# Revit family: Top hung and pivot window FAKRO FPU-V U5 preSelect
name_source: partatom
category: Okna
revit_build: Autodesk Revit 2015 (Build: 20140606_1530(x64)
units: mm (PartAtom-declared; Revit-internal decimal feet)

## types (9) — shared parameters
Apron Material = Fakro - aluminium RAL7022
Bimobject Category = Windows - Roof Windows
CSI MasterFormat 2016 Code = 08 60 00
CSI MasterFormat 2016 Title = Roof Windows and Skylights
CSI UniFormat II Code = B3020
CSI UniFormat II Title = Roof Openings
Glazing = Fakro - Glass
Handle Material = Fakro - handle
IFC Classification = Window
Kod zespołu = B3020110
Material External = Fakro - aluminium RAL7022
Material Internal = Fakro - frame - pinewood - RAL 9010
Model = FPU-V U5 preSelect
NBS Reference = 59-72
NBS Reference Description = Roof Window Units
Opis = Top hung and pivot window
Producent = FAKRO
UNSPC Category = Roofing accessories
UNSPC Code = 301516
URL = www.fakro.com
UV radiation EN 14351-1:2006+A1:2010 = 0.28
Uniclass 1.4 Code = JL11
Uniclass 1.4 Description = Rooflights/Roof windows
Uniclass 2.0 Code = PR-59-72
Uniclass 2.0 Description = Roof Window Units
Uniclass 2015 Code = Pr_30_59_72_77
Uniclass 2015 Title = Skylights
air inlet = V40P
air permeability class EN 14351-1:2006+A1:2010 = 4
colour = NCS S0502-Y (near to RAL 9010)
glass structure = 4HT-10-4H-10-4HT
glazing U-value [W/m2K] EN 14351-1:2006+A1:2010 = 0.5
impact resistance class EN 14351-1:2006+A1:2010 = 3
light transmittance factor tv EN 14351-1:2006+A1:2010 = 0.66
material = pinewood
opening method = top hung and pivot
operation mode = manual
reaction to fire EN 14351-1:2006+A1:2010 = D-s2;d2
resistance to snow load EN 14351-1:2006+A1:2010 = 4H-10-4H-10-4H
resistance to wind load EN 14351-1:2006+A1:2010 = C5/B5
roof angle = 15 – 55 (special version of the window 15 – 85)
solar factor [ g] EN 14351-1:2006+A1:2010 = 0.46
watertightness / unshielded (A) EN 14351-1:2006+A1:2010 = E900
window acoustic performance Rw [dB] EN 14351-1:2006+A1:2010 = 33(-2; -6)
window heat transfer coefficient Uw [W/m2K] EN 14351-1:2006+A1:2010 = 0.97

## per-type parameters (varying)
| type | Obj Type | Szerokość | Wysokość | air inlet efficiency - 10Pa | frame area | glass perimeter | glazing area | window internal area | window perimeter | window weight |
| FPU-V U5 preSelect - 02 - 55x98 | 2 mm  [stored 0.00656168 ft] | 547 mm | 981 mm  [stored 3.2185 ft] | 17 m³/h | 0.24 m² | 2320 mm | 0.29 m² | 0.41 m² | 3056 mm | 31.00 kg |
| FPU-V U5 preSelect - 03 - 66x98 | 3 mm  [stored 0.00984252 ft] | 657 mm | 981 mm  [stored 3.2185 ft] | 23 m³/h | 0.27 m² | 2540 mm  [stored 8.33333 ft] | 0.38 m² | 0.51 m² | 3276 mm  [stored 10.748 ft] | 36.00 kg |
| FPU-V U5 preSelect - 04 - 66x118 | 4 mm  [stored 0.0131234 ft] | 657 mm | 1181 mm  [stored 3.87467 ft] | 23 m³/h | 0.3 m² | 2940 mm  [stored 9.64567 ft] | 0.47 m² | 0.62 m² | 3676 mm | 40.00 kg |
| FPU-V U5 preSelect - 05 - 78x98 | 5 mm  [stored 0.0164042 ft] | 777 mm  [stored 2.54921 ft] | 981 mm  [stored 3.2185 ft] | 27 m³/h | 0.29 m² | 2780 mm  [stored 9.12073 ft] | 0.47 m² | 0.62 m² | 3516 mm  [stored 11.5354 ft] | 40.00 kg |
| FPU-V U5 preSelect - 06 - 78x118 | 6 mm  [stored 0.019685 ft] | 777 mm  [stored 2.54921 ft] | 1181 mm  [stored 3.87467 ft] | 27 m³/h | 0.32 m² | 3180 mm  [stored 10.4331 ft] | 0.59 m² | 0.75 m² | 3916 mm  [stored 12.8478 ft] | 46.00 kg |
| FPU-V U5 preSelect - 07 - 78x140 | 7 mm  [stored 0.0229659 ft] | 777 mm  [stored 2.54921 ft] | 1401 mm  [stored 4.59646 ft] | 27 m³/h | 0.36 m² | 3620 mm  [stored 11.8766 ft] | 0.73 m² | 0.91 m² | 4356 mm | 53.00 kg |
| FPU-V U5 preSelect - 08 - 94x118 | 8 mm  [stored 0.0262467 ft] | 937 mm  [stored 3.07415 ft] | 1181 mm  [stored 3.87467 ft] | 27 m³/h | 0.35 m² | 3500 mm | 0.75 m² | 0.93 m² | 4236 mm  [stored 13.8976 ft] | 53.00 kg |
| FPU-V U5 preSelect - 09 - 94x140 | 9 mm  [stored 0.0295276 ft] | 937 mm  [stored 3.07415 ft] | 1401 mm  [stored 4.59646 ft] | 27 m³/h | 0.43 m² | 4340 mm | 1.16 m² | 1.12 m² | 4676 mm | 61.00 kg |
| FPU-V U5 preSelect - 14 - 66x140 | 14 mm  [stored 0.0459318 ft] | 657 mm | 1401 mm  [stored 4.59646 ft] | 23 m³/h | 0.34 m² | 4340 mm | 0.58 m² | 0.75 m² | 4116 mm | 43.00 kg |

note: [stored X ft] marks values corroborated as IEEE doubles in the binary element streams (Revit-internal decimal feet)

## geometry (parser evidence)
native form markers: Sweep x2
no freeform markers — native parametric forms only
